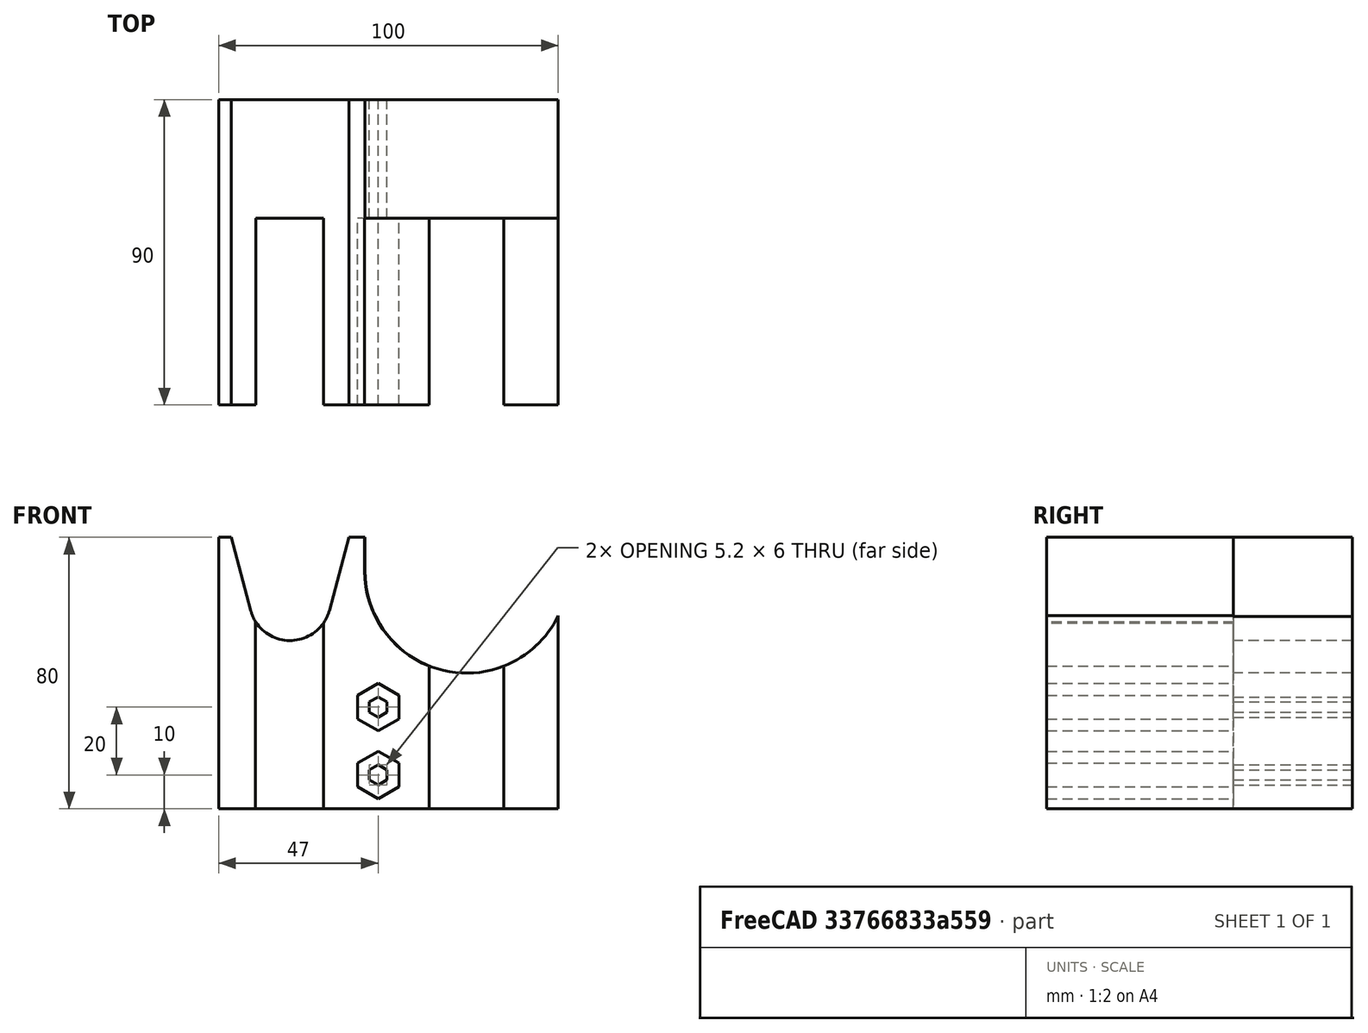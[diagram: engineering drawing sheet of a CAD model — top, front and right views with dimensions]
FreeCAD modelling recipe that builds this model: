
FCSTD DOCUMENT  (FreeCAD 0.19R)
Label: Hammers
License: All rights reserved
LicenseURL: http://en.wikipedia.org/wiki/All_rights_reserved
objects: Sketcher::SketchObject×9, PartDesign::Pocket×8, PartDesign::Chamfer×4, PartDesign::Pad×1, PartDesign::Body×1, Mesh::Feature×1
note: 36 computed .brp shape members not serialized (recipe doc carries the construction recipe); baked Part::Feature solids carry a one-line shape summary decoded from their .brp

FEATURE [Sketcher::SketchObject] Sketch
  FullyConstrained = true
  MapMode = 5
  Placement = pos=(0,0,0) rot=(1,0,0;1.5708rad)
  Support = -> [XZ_Plane]
  sketch-geometry (4):
    g0: LineSegment StartX=-50 StartY=0 StartZ=0 EndX=50 EndY=0 EndZ=0
    g1: LineSegment StartX=50 StartY=0 StartZ=0 EndX=50 EndY=-80 EndZ=0
    g2: LineSegment StartX=50 StartY=-80 StartZ=0 EndX=-50 EndY=-80 EndZ=0
    g3: LineSegment StartX=-50 StartY=-80 StartZ=0 EndX=-50 EndY=0 EndZ=0
  constraints (11):
    c: Coincident(g0,g1)
    c: Coincident(g1,g2)
    c: Coincident(g2,g3)
    c: Coincident(g3,g0)
    c: Horizontal(g0)
    c: Vertical(g1)
    c: Vertical(g3)
    c: PointOnObject(g0,g-1)
    c: Symmetric(g1,g2,g-2)
    c: Distance(g2) = 100
    c: Distance(g1) = 80
FEATURE [PartDesign::Pad] Pad
  Direction = (1,1,1)
  Length = 90
  Length2 = 100
  Placement = pos=(0,0,0) rot=(1,0,0;1.5708rad)
  Profile = -> Sketch
  Type = 0
FEATURE [Sketcher::SketchObject] Sketch001
  FullyConstrained = false
  MapMode = 5
  Placement = pos=(0,-90,3.98e-14) rot=(1,0,0;1.5708rad)
  Support = -> [Pad]
  sketch-geometry (8):
    g0: LineSegment StartX=34 StartY=-96.3962 StartZ=0 EndX=34 EndY=-37.9106 EndZ=0
    g1: LineSegment StartX=12 StartY=-96.3962 StartZ=0 EndX=12 EndY=-37.9106 EndZ=0
    g2: ArcOfCircle CenterX=23 CenterY=-10 CenterZ=0 NormalX=0 NormalY=0 NormalZ=1 AngleXU=0 Radius=30 StartAngle=5.08781 EndAngle=6.28319
    g3: ArcOfCircle CenterX=23 CenterY=-10 CenterZ=0 NormalX=0 NormalY=0 NormalZ=1 AngleXU=0 Radius=30 StartAngle=3.14159 EndAngle=4.33697
    g4: LineSegment StartX=-7 StartY=-10 StartZ=0 EndX=-7 EndY=21.1525 EndZ=0
    g5: LineSegment StartX=53 StartY=-10 StartZ=0 EndX=53 EndY=28.5099 EndZ=0
    g6: LineSegment StartX=-7 StartY=21.1525 StartZ=0 EndX=53 EndY=28.5099 EndZ=0
    g7: LineSegment StartX=12 StartY=-96.3962 StartZ=0 EndX=34 EndY=-96.3962 EndZ=0
  constraints (20):
    c: Vertical(g0)
    c: Vertical(g1)
    c: Coincident(g2,g0)
    c: Coincident(g3,g2)
    c: Coincident(g3,g1)
    c: Distance(g0,g1) = 22
    c: Radius(g3) = 30
    c: Radius(g2) = 30
    c: DistanceY(g1,g0) = 0
    c: Vertical(g4)
    c: Vertical(g5)
    c: Tangent(g5,g2) = -1.5708
    c: Tangent(g4,g3) = 1.5708
    c: Coincident(g6,g4)
    c: Coincident(g5,g6)
    c: Coincident(g7,g1)
    c: Coincident(g7,g0)
    c: Horizontal(g7)
    c: DistanceY(g2) = -10
    c: DistanceX(g2) = 23
FEATURE [PartDesign::Pocket] Pocket
  BaseFeature = -> Pad
  Length = 55
  Length2 = 100
  Placement = pos=(0,0,0) rot=(1,0,0;1.5708rad)
  Profile = -> Sketch001
  Type = 0
FEATURE [Sketcher::SketchObject] Sketch002
  FullyConstrained = false
  MapMode = 5
  Placement = pos=(2.4e-15,-35,3.4e-14) rot=(1,0,0;1.5708rad)
  Support = -> [Pocket]
  sketch-geometry (4):
    g0: ArcOfCircle CenterX=23 CenterY=-10 CenterZ=0 NormalX=0 NormalY=0 NormalZ=1 AngleXU=0 Radius=30 StartAngle=3.14159 EndAngle=6.35161
    g1: LineSegment StartX=-7 StartY=-10 StartZ=0 EndX=-7 EndY=15.153 EndZ=0
    g2: LineSegment StartX=52.9298 StartY=-7.94878 StartZ=0 EndX=50.0407 EndY=19.3941 EndZ=0
    g3: LineSegment StartX=50.0407 StartY=19.3941 StartZ=0 EndX=-7 EndY=15.153 EndZ=0
  constraints (8):
    c: Coincident(g2,g0)
    c: Coincident(g3,g2)
    c: Coincident(g3,g1)
    c: Tangent(g1,g0) = 1.5708
    c: Radius(g0) = 30
    c: Vertical(g1)
    c: DistanceY(g0) = -10
    c: DistanceX(g0) = 23
FEATURE [PartDesign::Pocket] Pocket001
  BaseFeature = -> Pocket
  Length = 5
  Length2 = 100
  Placement = pos=(0,0,0) rot=(1,0,0;1.5708rad)
  Profile = -> Sketch002
  Type = 1
FEATURE [Sketcher::SketchObject] Sketch003
  FullyConstrained = false
  MapMode = 5
  Placement = pos=(-50,0,0) rot=(0.707107,0,-0.707107;3.14159rad)
  Support = -> [Pocket001]
  sketch-geometry (4):
    g0: LineSegment StartX=-39.1637 StartY=-25 StartZ=0 EndX=-19.1637 EndY=-25 EndZ=0
    g1: LineSegment StartX=-19.1637 StartY=-25 StartZ=0 EndX=-19.1637 EndY=-87.8011 EndZ=0
    g2: LineSegment StartX=-19.1637 StartY=-87.8011 StartZ=0 EndX=-39.1637 EndY=-87.8011 EndZ=0
    g3: LineSegment StartX=-39.1637 StartY=-87.8011 StartZ=0 EndX=-39.1637 EndY=-25 EndZ=0
  constraints (10):
    c: Coincident(g0,g1)
    c: Coincident(g1,g2)
    c: Coincident(g2,g3)
    c: Coincident(g3,g0)
    c: Horizontal(g0)
    c: Horizontal(g2)
    c: Vertical(g1)
    c: Vertical(g3)
    c: Distance(g2) = 20
    c: DistanceY(g0) = -25
FEATURE [PartDesign::Pocket] Pocket002
  BaseFeature = -> Pocket001
  Length = 55
  Length2 = 100
  Placement = pos=(0,0,0) rot=(1,0,0;1.5708rad)
  Profile = -> Sketch003
  Type = 0
FEATURE [Sketcher::SketchObject] Sketch004
  FullyConstrained = false
  MapMode = 5
  Placement = pos=(-50,0,0) rot=(0.707107,0,-0.707107;3.14159rad)
  Support = -> [Pocket002]
  sketch-geometry (4):
    g0: ArcOfCircle CenterX=-28.9845 CenterY=-18.401 CenterZ=0 NormalX=0 NormalY=0 NormalZ=1 AngleXU=0 Radius=12 StartAngle=3.40339 EndAngle=6.02139
    g1: LineSegment StartX=-40.5756 StartY=-21.5069 StartZ=0 EndX=-48.9535 EndY=9.76004 EndZ=0
    g2: LineSegment StartX=-17.3934 StartY=-21.5069 StartZ=0 EndX=-9.26047 EndY=8.84549 EndZ=0
    g3: LineSegment StartX=-48.9535 StartY=9.76004 StartZ=0 EndX=-9.26047 EndY=8.84549 EndZ=0
  constraints (7):
    c: Coincident(g3,g1)
    c: Coincident(g3,g2)
    c: Tangent(g1,g0) = 1.5708
    c: Tangent(g2,g0) = -1.5708
    c: DistanceY(g0,g0) = 0
    c: Radius(g0) = 12
    c: Angle(g2) = 1.309
FEATURE [PartDesign::Pocket] Pocket003
  BaseFeature = -> Pocket002
  Length = 5
  Length2 = 100
  Placement = pos=(0,0,0) rot=(1,0,0;1.5708rad)
  Profile = -> Sketch004
  Type = 1
FEATURE [Sketcher::SketchObject] Sketch005
  FullyConstrained = true
  MapMode = 5
  Placement = pos=(0,-90,2.2e-13) rot=(1,0,0;1.5708rad)
  Support = -> [Pocket003]
  sketch-geometry (14):
    g0: LineSegment StartX=-3 StartY=-57 StartZ=0 EndX=3.06218 EndY=-53.5 EndZ=0
    g1: LineSegment StartX=3.06218 StartY=-53.5 StartZ=0 EndX=3.06218 EndY=-46.5 EndZ=0
    g2: LineSegment StartX=3.06218 StartY=-46.5 StartZ=0 EndX=-3 EndY=-43 EndZ=0
    g3: LineSegment StartX=-3 StartY=-43 StartZ=0 EndX=-9.06218 EndY=-46.5 EndZ=0
    g4: LineSegment StartX=-9.06218 StartY=-46.5 StartZ=0 EndX=-9.06218 EndY=-53.5 EndZ=0
    g5: LineSegment StartX=-9.06218 StartY=-53.5 StartZ=0 EndX=-3 EndY=-57 EndZ=0
    g6: Circle CenterX=-3 CenterY=-50 CenterZ=0 NormalX=0 NormalY=0 NormalZ=1 AngleXU=0 Radius=7
    g7: LineSegment StartX=3.06218 StartY=-73.5 StartZ=0 EndX=3.06218 EndY=-66.5 EndZ=0
    g8: LineSegment StartX=3.06218 StartY=-66.5 StartZ=0 EndX=-3 EndY=-63 EndZ=0
    g9: LineSegment StartX=-3 StartY=-63 StartZ=0 EndX=-9.06218 EndY=-66.5 EndZ=0
    g10: LineSegment StartX=-9.06218 StartY=-66.5 StartZ=0 EndX=-9.06218 EndY=-73.5 EndZ=0
    g11: LineSegment StartX=-9.06218 StartY=-73.5 StartZ=0 EndX=-3 EndY=-77 EndZ=0
    g12: LineSegment StartX=-3 StartY=-77 StartZ=0 EndX=3.06218 EndY=-73.5 EndZ=0
    g13: Circle CenterX=-3 CenterY=-70 CenterZ=0 NormalX=0 NormalY=0 NormalZ=1 AngleXU=0 Radius=7
  constraints (34):
    c: Coincident(g0,g1)
    c: Coincident(g1,g2)
    c: Coincident(g2,g3)
    c: Coincident(g3,g4)
    c: Coincident(g4,g5)
    c: Coincident(g5,g0)
    c: Equal(g0, g1-g5) x5
    c: PointOnObject(g0,g6)
    c: PointOnObject(g1,g6)
    c: PointOnObject(g2,g6)
    c: PointOnObject(g3,g6)
    c: PointOnObject(g4,g6)
    c: PointOnObject(g5,g6)
    c: Coincident(g7,g8)
    c: Coincident(g8,g9)
    c: Coincident(g9,g10)
    c: Coincident(g10,g11)
    c: Coincident(g11,g12)
    c: Coincident(g12,g7)
    c: Equal(g7, g8-g12) x5
    c: PointOnObject(g7,g13)
    c: PointOnObject(g8,g13)
    c: PointOnObject(g9,g13)
    c: PointOnObject(g10,g13)
    c: PointOnObject(g11,g13)
    c: PointOnObject(g12,g13)
    c: Vertical(g7)
    c: Vertical(g1)
    c: DistanceX(g6) = -3
    c: DistanceX(g13) = -3
    c: Radius(g6) = 7
    c: Equal(g6,g13)
    c: Distance(g6,g13) = 20
    c: DistanceY(g6) = -50
FEATURE [Sketcher::SketchObject] Sketch006
  FullyConstrained = true
  MapMode = 5
  Placement = pos=(0,-35,1.1e-13) rot=(1,0,0;1.5708rad)
  sketch-geometry (14):
    g0: LineSegment StartX=-3 StartY=-53 StartZ=0 EndX=-0.401924 EndY=-51.5 EndZ=0
    g1: LineSegment StartX=-0.401924 StartY=-51.5 StartZ=0 EndX=-0.401924 EndY=-48.5 EndZ=0
    g2: LineSegment StartX=-0.401924 StartY=-48.5 StartZ=0 EndX=-3 EndY=-47 EndZ=0
    g3: LineSegment StartX=-3 StartY=-47 StartZ=0 EndX=-5.59808 EndY=-48.5 EndZ=0
    g4: LineSegment StartX=-5.59808 StartY=-48.5 StartZ=0 EndX=-5.59808 EndY=-51.5 EndZ=0
    g5: LineSegment StartX=-5.59808 StartY=-51.5 StartZ=0 EndX=-3 EndY=-53 EndZ=0
    g6: Circle CenterX=-3 CenterY=-50 CenterZ=0 NormalX=0 NormalY=0 NormalZ=1 AngleXU=0 Radius=3
    g7: LineSegment StartX=-3 StartY=-73 StartZ=0 EndX=-0.401924 EndY=-71.5 EndZ=0
    g8: LineSegment StartX=-0.401924 StartY=-71.5 StartZ=0 EndX=-0.401924 EndY=-68.5 EndZ=0
    g9: LineSegment StartX=-0.401924 StartY=-68.5 StartZ=0 EndX=-3 EndY=-67 EndZ=0
    g10: LineSegment StartX=-3 StartY=-67 StartZ=0 EndX=-5.59808 EndY=-68.5 EndZ=0
    g11: LineSegment StartX=-5.59808 StartY=-68.5 StartZ=0 EndX=-5.59808 EndY=-71.5 EndZ=0
    g12: LineSegment StartX=-5.59808 StartY=-71.5 StartZ=0 EndX=-3 EndY=-73 EndZ=0
    g13: Circle CenterX=-3 CenterY=-70 CenterZ=0 NormalX=0 NormalY=0 NormalZ=1 AngleXU=0 Radius=3
  constraints (34):
    c: Coincident(g0,g1)
    c: Coincident(g1,g2)
    c: Coincident(g2,g3)
    c: Coincident(g3,g4)
    c: Coincident(g4,g5)
    c: Coincident(g5,g0)
    c: Equal(g0, g1-g5) x5
    c: PointOnObject(g0,g6)
    c: PointOnObject(g1,g6)
    c: PointOnObject(g2,g6)
    c: PointOnObject(g3,g6)
    c: PointOnObject(g4,g6)
    c: PointOnObject(g5,g6)
    c: Coincident(g7,g8)
    c: Coincident(g8,g9)
    c: Coincident(g9,g10)
    c: Coincident(g10,g11)
    c: Coincident(g11,g12)
    c: Coincident(g12,g7)
    c: Equal(g7, g8-g12) x5
    c: PointOnObject(g7,g13)
    c: PointOnObject(g8,g13)
    c: PointOnObject(g9,g13)
    c: PointOnObject(g10,g13)
    c: PointOnObject(g11,g13)
    c: PointOnObject(g12,g13)
    c: Vertical(g8)
    c: Vertical(g1)
    c: Distance(g13,g6) = 20
    c: DistanceY(g6) = -50
    c: Radius(g6) = 3
    c: Equal(g6,g13)
    c: DistanceX(g6) = -3
    c: DistanceX(g13) = -3
FEATURE [PartDesign::Pocket] Pocket004
  BaseFeature = -> Pocket003
  Length = 55
  Length2 = 100
  Placement = pos=(0,0,0) rot=(1,0,0;1.5708rad)
  Profile = -> Sketch005
  Type = 0
FEATURE [PartDesign::Pocket] Pocket005
  BaseFeature = -> Pocket004
  Length = 5
  Length2 = 100
  Placement = pos=(0,0,0) rot=(1,0,0;1.5708rad)
  Profile = -> Sketch006
  Type = 1
FEATURE [Sketcher::SketchObject] Sketch007
  FullyConstrained = false
  MapMode = 5
  Placement = pos=(0,-90,3.98e-14) rot=(1,0,0;1.5708rad)
  Support = -> [Pocket005]
  sketch-geometry (4):
    g0: LineSegment StartX=-40 StartY=-36.8247 StartZ=0 EndX=-18 EndY=-36.8247 EndZ=0
    g1: LineSegment StartX=-18 StartY=-36.8247 StartZ=0 EndX=-18 EndY=-100.026 EndZ=0
    g2: LineSegment StartX=-18 StartY=-100.026 StartZ=0 EndX=-40 EndY=-100.026 EndZ=0
    g3: LineSegment StartX=-40 StartY=-100.026 StartZ=0 EndX=-40 EndY=-36.8247 EndZ=0
  constraints (10):
    c: Coincident(g0,g1)
    c: Coincident(g1,g2)
    c: Coincident(g2,g3)
    c: Coincident(g3,g0)
    c: Horizontal(g0)
    c: Horizontal(g2)
    c: Vertical(g1)
    c: Vertical(g3)
    c: Distance(g0) = 22
    c: DistanceX(g0) = -18
FEATURE [PartDesign::Pocket] Pocket006
  BaseFeature = -> Pocket005
  Length = 55
  Length2 = 100
  Placement = pos=(0,0,0) rot=(1,0,0;1.5708rad)
  Profile = -> Sketch007
  Type = 0
FEATURE [Sketcher::SketchObject] Sketch009
  FullyConstrained = false
  MapMode = 5
  Placement = pos=(0,-90,3.98e-14) rot=(1,0,0;1.5708rad)
  Support = -> [Pocket006]
  sketch-geometry (4):
    g0: ArcOfCircle CenterX=-28.9699 CenterY=-32.3752 CenterZ=0 NormalX=0 NormalY=0 NormalZ=1 AngleXU=0 Radius=12 StartAngle=3.31653 EndAngle=6.10825
    g1: LineSegment StartX=-40.7868 StartY=-34.4638 StartZ=0 EndX=-48.3653 EndY=8.41521 EndZ=0
    g2: LineSegment StartX=-17.1531 StartY=-34.4638 StartZ=0 EndX=-9.68932 EndY=7.76602 EndZ=0
    g3: LineSegment StartX=-48.3653 StartY=8.41521 StartZ=0 EndX=-9.68932 EndY=7.76602 EndZ=0
  constraints (6):
    c: Radius(g0) = 12
    c: Coincident(g3,g1)
    c: Coincident(g3,g2)
    c: Tangent(g1,g0) = 1.5708
    c: Tangent(g2,g0) = -1.5708
    c: DistanceY(g0,g0) = 0
FEATURE [PartDesign::Pocket] Pocket007
  BaseFeature = -> Pocket006
  Length = 41
  Length2 = 100
  Placement = pos=(0,0,0) rot=(1,0,0;1.5708rad)
  Profile = -> Sketch009
  Type = 1
FEATURE [PartDesign::Chamfer] Chamfer
  Angle = 45
  Base = -> Pocket007 [Face6]
  BaseFeature = -> Pocket007
  ChamferType = 0
  FlipDirection = false
  Placement = pos=(0,0,0) rot=(1,0,0;1.5708rad)
  Size = 2
  Size2 = 1
  SupportTransform = false
FEATURE [PartDesign::Chamfer] Chamfer001
  Angle = 45
  Base = -> Chamfer [Edge26]
  BaseFeature = -> Chamfer
  ChamferType = 0
  FlipDirection = false
  Placement = pos=(0,0,0) rot=(1,0,0;1.5708rad)
  Size = 6
  Size2 = 1
  SupportTransform = false
FEATURE [PartDesign::Chamfer] Chamfer002
  Angle = 45
  Base = -> Chamfer001 [Face33]
  BaseFeature = -> Chamfer001
  ChamferType = 0
  FlipDirection = false
  Placement = pos=(0,0,0) rot=(1,0,0;1.5708rad)
  Size = 1
  Size2 = 1
  SupportTransform = false
FEATURE [PartDesign::Chamfer] Chamfer003
  Angle = 45
  Base = -> Chamfer002 [Face44]
  BaseFeature = -> Chamfer002
  ChamferType = 0
  FlipDirection = false
  Placement = pos=(0,0,0) rot=(1,0,0;1.5708rad)
  Size = 1
  Size2 = 1
  SupportTransform = false
FEATURE [PartDesign::Body] Body
  Group = -> [Sketch,Pad,Sketch001,Pocket,Sketch002,Pocket001,Sketch003,Pocket002,Sketch004,Pocket003,Sketch005,Sketch006,Pocket004,Pocket005,Sketch007,Pocket006,Sketch009,Pocket007,Chamfer,Chamfer001,Chamfer002,Chamfer003]
  Origin = -> Origin
  Tip = -> Chamfer003
FEATURE [Mesh::Feature] Mesh  label="Chamfer003 (Meshed)"
